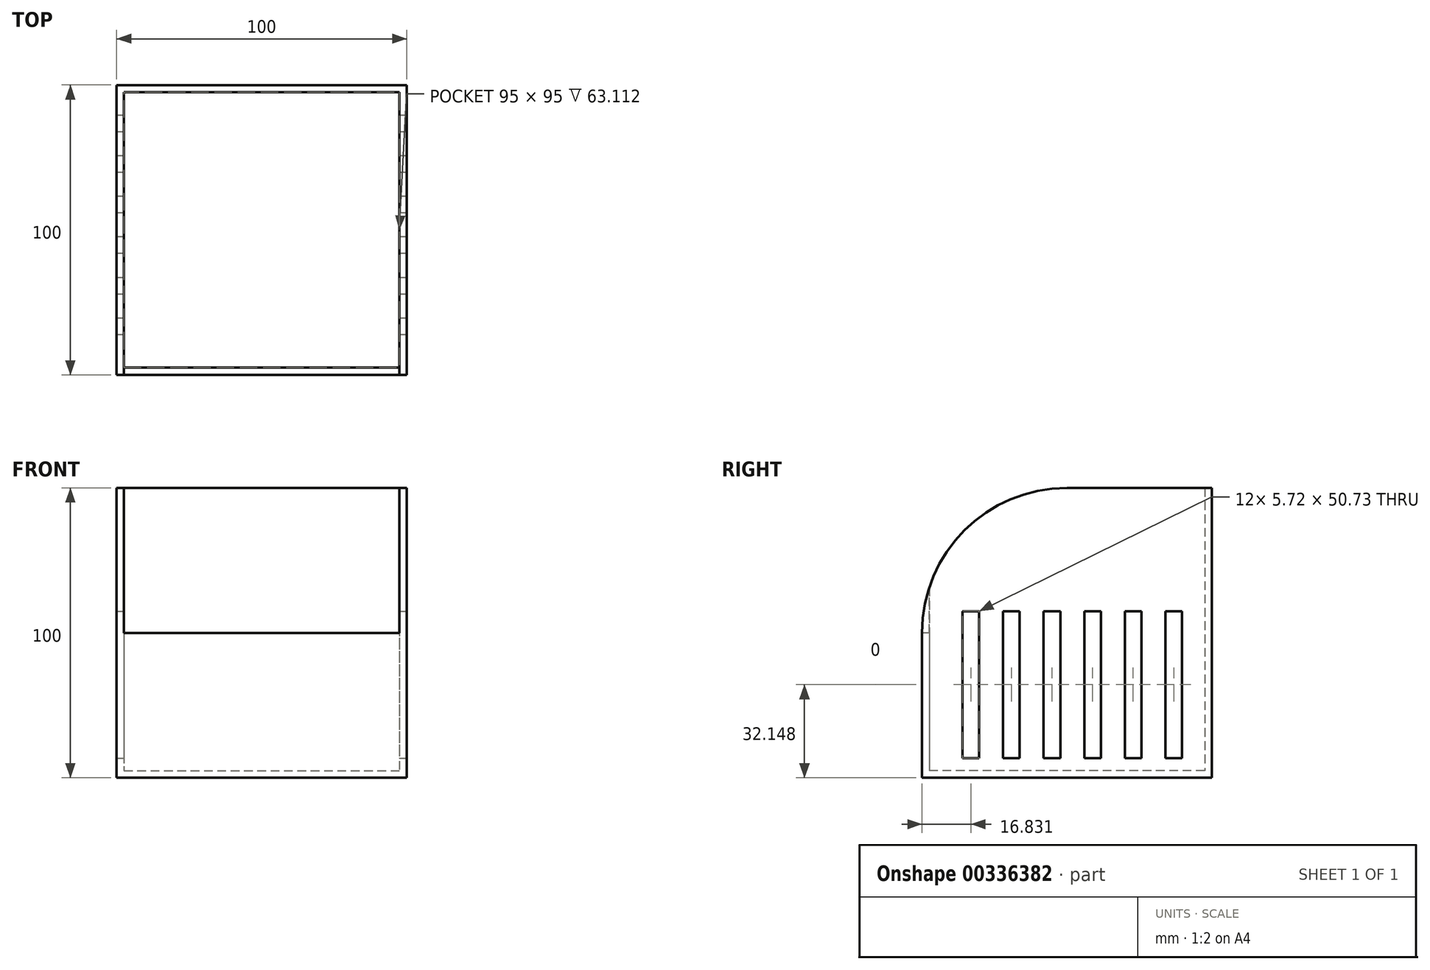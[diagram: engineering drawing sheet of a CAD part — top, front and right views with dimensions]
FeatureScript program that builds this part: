
annotation { "Feature Type Name" : "Feature", "Feature Type Description" : "" }
export const myFeature = defineFeature(function(context is Context, id is Id, definition is map)
    precondition{}
    {
        {
            var Q0;
            Q0=qCreatedBy(makeId("Top.planeOp"),FACE);
            var sketch = newSketch(context, id + "F0", { "sketchPlane" : qUnion([Q0])});
            skLineSegment(sketch, "E0.bottom", {"start": v(-58.54, 49.5) * mm, "end": v(41.46, 49.5) * mm});
            skLineSegment(sketch, "E0.top", {"start": v(-58.54, -50.5) * mm, "end": v(41.46, -50.5) * mm});
            skLineSegment(sketch, "E0.left", {"start": v(-58.54, 49.5) * mm, "end": v(-58.54, -50.5) * mm});
            skLineSegment(sketch, "E0.right", {"start": v(41.46, 49.5) * mm, "end": v(41.46, -50.5) * mm});
            skSolve(sketch);
        }
        {
            var Q0;
            Q0=makeQuery(id+"F0.imprint","IMPRINT",FACE,{"disambiguationData":[TD([[makeQuery(id+"F0.imprint","IMPRINT",EDGE,{"derivedFrom":sQuery(id+"F0.wireOp",EDGE,"E0.bottom")}),-1.0]])]});
            extrude(context, id + "F1", {"entities" : qUnion([Q0]), "depth" : 100 * mm});
        }
        {
            var Q0;
            Q0=makeQuery(id+"F1.opExtrude","CAP_FACE",FACE,{"disambiguationData":[OSD([sQuery(id+"F0.wireOp",EDGE,"E0.bottom"),sQuery(id+"F0.wireOp",EDGE,"E0.top"),sQuery(id+"F0.wireOp",EDGE,"E0.left"),sQuery(id+"F0.wireOp",EDGE,"E0.right")])],"isStart":false});
            shell(context, id + "F2", {"entities" : qUnion([Q0]), "thickness" : 2.5 * mm});
        }
        {
            var Q0;
            Q0=makeQuery(id+"F1.opExtrude","CAP_FACE",FACE,{"disambiguationData":[OSD([sQuery(id+"F0.wireOp",EDGE,"E0.bottom"),sQuery(id+"F0.wireOp",EDGE,"E0.top"),sQuery(id+"F0.wireOp",EDGE,"E0.left"),sQuery(id+"F0.wireOp",EDGE,"E0.right")])],"isStart":false});
            var sketch = newSketch(context, id + "F3", { "sketchPlane" : qUnion([Q0])});
            skLineSegment(sketch, "E1.bottom", {"start": v(-56.04, -33.05) * mm, "end": v(38.9, -33.05) * mm});
            skLineSegment(sketch, "E1.top", {"start": v(-56.04, -56.93) * mm, "end": v(38.9, -56.93) * mm});
            skLineSegment(sketch, "E1.left", {"start": v(-56.04, -33.05) * mm, "end": v(-56.04, -56.93) * mm});
            skLineSegment(sketch, "E1.right", {"start": v(38.9, -33.05) * mm, "end": v(38.9, -56.93) * mm});
            skSolve(sketch);
        }
        {
            var Q0;
            {var subQ0=sQuery(id+"F3.wireOp",EDGE,"E1.left");var subQ1=sQuery(id+"F0.wireOp",EDGE,"E0.top");var subQ2=makeQuery(id+"F1.opExtrude","CAP_EDGE",EDGE,{"disambiguationData":[OSD([subQ1])],"isStart":false});var subQ5=makeQuery(id+"F3.imprint","INTERSECT",VERTEX,{"derivedFrom":[subQ2,subQ0]});Q0=makeQuery(id+"F3.imprint","IMPRINT",FACE,{"disambiguationData":[TD([[makeQuery(id+"F3.imprint","IMPRINT",EDGE,{"disambiguationData":[TD([[subQ5,-1.0]])],"derivedFrom":subQ2}),1.0]])]});}
            extrude(context, id + "F4", {"entities" : qUnion([Q0]), "operationType" : NewBodyOperationType.REMOVE, "oppositeDirection" : true, "depth" : 50 * mm});
        }
        {
            var Q0;
            {var subQ0=sQuery(id+"F0.wireOp",EDGE,"E0.left");var subQ1=sQuery(id+"F0.wireOp",EDGE,"E0.top");Q0=makeQuery(id+"F4.boolean.opBoolean","SPLIT",EDGE,{"disambiguationData":[TD([makeQuery(id+"F1.opExtrude","SWEPT_FACE",FACE,{"disambiguationData":[OSD([subQ0])]})])],"derivedFrom":makeQuery(id+"F1.opExtrude","CAP_EDGE",EDGE,{"disambiguationData":[OSD([subQ1])],"isStart":false})});}
            var Q1;
            {var subQ0=sQuery(id+"F0.wireOp",EDGE,"E0.right");var subQ1=sQuery(id+"F0.wireOp",EDGE,"E0.top");Q1=makeQuery(id+"F4.boolean.opBoolean","SPLIT",EDGE,{"disambiguationData":[TD([makeQuery(id+"F1.opExtrude","SWEPT_FACE",FACE,{"disambiguationData":[OSD([subQ0])]})])],"derivedFrom":makeQuery(id+"F1.opExtrude","CAP_EDGE",EDGE,{"disambiguationData":[OSD([subQ1])],"isStart":false})});}
            fillet(context, id + "F5", {"entities" : qUnion([Q0, Q1]), "radius" : 50 * mm, "tangentPropagation" : true, "allowEdgeOverflow" : false});
        }
        {
            var Q0;
            Q0=makeQuery(id+"F1.opExtrude","SWEPT_FACE",FACE,{"disambiguationData":[OSD([sQuery(id+"F0.wireOp",EDGE,"E0.right")])]});
            var sketch = newSketch(context, id + "F6", { "sketchPlane" : qUnion([Q0])});
            skLineSegment(sketch, "E2.bottom", {"start": v(-36.53, 57.52) * mm, "end": v(-30.8, 57.52) * mm});
            skLineSegment(sketch, "E2.top", {"start": v(-36.53, 6.78) * mm, "end": v(-30.8, 6.78) * mm});
            skLineSegment(sketch, "E2.left", {"start": v(-36.53, 57.52) * mm, "end": v(-36.53, 6.78) * mm});
            skLineSegment(sketch, "E2.right", {"start": v(-30.8, 57.52) * mm, "end": v(-30.8, 6.78) * mm});
            skLineSegment(sketch, "E3.1.0.0", {"start": v(-22.53, 57.52) * mm, "end": v(-16.8, 57.52) * mm});
            skLineSegment(sketch, "E3.1.0.1", {"start": v(-16.8, 57.52) * mm, "end": v(-16.8, 6.78) * mm});
            skLineSegment(sketch, "E3.1.0.2", {"start": v(-22.53, 57.52) * mm, "end": v(-22.53, 6.78) * mm});
            skLineSegment(sketch, "E3.1.0.3", {"start": v(-22.53, 6.78) * mm, "end": v(-16.8, 6.78) * mm});
            skLineSegment(sketch, "E3.2.0.0", {"start": v(-8.53, 57.52) * mm, "end": v(-2.8, 57.52) * mm});
            skLineSegment(sketch, "E3.2.0.1", {"start": v(-2.8, 57.52) * mm, "end": v(-2.8, 6.78) * mm});
            skLineSegment(sketch, "E3.2.0.2", {"start": v(-8.53, 57.52) * mm, "end": v(-8.53, 6.78) * mm});
            skLineSegment(sketch, "E3.2.0.3", {"start": v(-8.53, 6.78) * mm, "end": v(-2.8, 6.78) * mm});
            skLineSegment(sketch, "E3.3.0.0", {"start": v(5.47, 57.52) * mm, "end": v(11.2, 57.52) * mm});
            skLineSegment(sketch, "E3.3.0.1", {"start": v(11.2, 57.52) * mm, "end": v(11.2, 6.78) * mm});
            skLineSegment(sketch, "E3.3.0.2", {"start": v(5.47, 57.52) * mm, "end": v(5.47, 6.78) * mm});
            skLineSegment(sketch, "E3.3.0.3", {"start": v(5.47, 6.78) * mm, "end": v(11.2, 6.78) * mm});
            skLineSegment(sketch, "E3.4.0.0", {"start": v(19.47, 57.52) * mm, "end": v(25.2, 57.52) * mm});
            skLineSegment(sketch, "E3.4.0.1", {"start": v(25.2, 57.52) * mm, "end": v(25.2, 6.78) * mm});
            skLineSegment(sketch, "E3.4.0.2", {"start": v(19.47, 57.52) * mm, "end": v(19.47, 6.78) * mm});
            skLineSegment(sketch, "E3.4.0.3", {"start": v(19.47, 6.78) * mm, "end": v(25.2, 6.78) * mm});
            skLineSegment(sketch, "E3.5.0.0", {"start": v(33.47, 57.52) * mm, "end": v(39.2, 57.52) * mm});
            skLineSegment(sketch, "E3.5.0.1", {"start": v(39.2, 57.52) * mm, "end": v(39.2, 6.78) * mm});
            skLineSegment(sketch, "E3.5.0.2", {"start": v(33.47, 57.52) * mm, "end": v(33.47, 6.78) * mm});
            skLineSegment(sketch, "E3.5.0.3", {"start": v(33.47, 6.78) * mm, "end": v(39.2, 6.78) * mm});
            skLineSegment(sketch, "E3.direction1", {"start": v(-36.53, 6.78) * mm, "end": v(-22.53, 6.78) * mm, "construction": true});
            skSolve(sketch);
        }
        {
            var Q0;
            Q0=makeQuery(id+"F6.imprint","IMPRINT",FACE,{"disambiguationData":[TD([[makeQuery(id+"F6.imprint","IMPRINT",EDGE,{"derivedFrom":sQuery(id+"F6.wireOp",EDGE,"E2.bottom")}),-1.0]])]});
            var Q1;
            Q1=makeQuery(id+"F6.imprint","IMPRINT",FACE,{"disambiguationData":[TD([[makeQuery(id+"F6.imprint","IMPRINT",EDGE,{"derivedFrom":sQuery(id+"F6.wireOp",EDGE,"E3.1.0.0")}),-1.0]])]});
            var Q2;
            Q2=makeQuery(id+"F6.imprint","IMPRINT",FACE,{"disambiguationData":[TD([[makeQuery(id+"F6.imprint","IMPRINT",EDGE,{"derivedFrom":sQuery(id+"F6.wireOp",EDGE,"E3.2.0.0")}),-1.0]])]});
            var Q3;
            Q3=makeQuery(id+"F6.imprint","IMPRINT",FACE,{"disambiguationData":[TD([[makeQuery(id+"F6.imprint","IMPRINT",EDGE,{"derivedFrom":sQuery(id+"F6.wireOp",EDGE,"E3.3.0.0")}),-1.0]])]});
            var Q4;
            Q4=makeQuery(id+"F6.imprint","IMPRINT",FACE,{"disambiguationData":[TD([[makeQuery(id+"F6.imprint","IMPRINT",EDGE,{"derivedFrom":sQuery(id+"F6.wireOp",EDGE,"E3.4.0.0")}),-1.0]])]});
            var Q5;
            Q5=makeQuery(id+"F6.imprint","IMPRINT",FACE,{"disambiguationData":[TD([[makeQuery(id+"F6.imprint","IMPRINT",EDGE,{"derivedFrom":sQuery(id+"F6.wireOp",EDGE,"E3.5.0.0")}),-1.0]])]});
            extrude(context, id + "F7", {"entities" : qUnion([Q0, Q1, Q2, Q3, Q4, Q5]), "operationType" : NewBodyOperationType.REMOVE, "endBound" : BoundingType.THROUGH_ALL, "oppositeDirection" : true, "depth" : 25 * mm});
        }
    });
